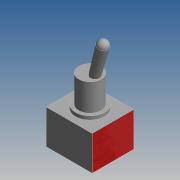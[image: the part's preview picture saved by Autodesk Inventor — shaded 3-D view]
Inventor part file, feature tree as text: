
AUTODESK INVENTOR PART (.ipt)
format: ipt  version: 2015 SP1 (Build 190203100, 203)  size: 225,792 bytes
history: native  units: mm
features: sketch x4, extrude x3, revolve x1, fillet x1
ambient origin geometry x8: Origin, YZ Plane, XZ Plane, XY Plane, X Axis, Y Axis, Z Axis, Center Point
bodies: Solid1 (feature_tree)
feature tree (9):
  extrude  "Extrusion1"  Depth=11.5mm
  extrude  "Extrusion2"  Depth=9.5mm
  extrude  "Extrusion3"  Depth=1.0mm
  revolve  "Revolution1"  Angle=15.0deg
  fillet  "Fillet1"  Radius=5.0mm
  sketch  "Sketch1"  dims[d0=12.7mm d1=11.5mm]
  sketch  "Sketch2"  dims[d2=9.5mm d3=0.0mm d4=8.0mm]
  sketch  "Sketch3"  dims[d5=1.0mm d6=0.0mm d7=6.2mm]
  sketch  "Sketch4"  dims[d8=7.5mm d9=0.0mm d10=15.0deg d11=5.0mm d13=10.0mm d14=3.0mm d16=2.5mm d17=90.0deg d18=1.4mm]
